# Revit family: Haworth_BeHold_Modular_SlimPedestal
name_source: partatom
category: Furniture Systems
revit_build: Autodesk Revit 2018 (Build: 20170223_1515(x64)
units: mm (PartAtom-declared; Revit-internal decimal feet)

## family parameters
Always vertical = Yes
Cut with Voids When Loaded = No
OmniClass Number = 23.40.70.14.64.21
OmniClass Title = Systems Furniture
Part Type = Normal
Room Calculation Point = No
Round Connector Dimension = Use Diameter
Shared = No
Work Plane-Based = No

## types (6) — shared parameters
Actual Leg Control = No
Actual Width = 12"
Assembly Code = E2020200
Back Case Back Control = 0"
Case Thickness = 3/4"
Caster Back Offset = 1 3/16"
Caster Finish = Haworth _ Polymer _ Slate
Caster Front Offset = 1 7/8"
Casters Side Offset = 1 9/16"
Custom Size = No
Drawer Height = 4 1/8"
Drawer Width = 10 9/32"
Glide Finish = Haworth _ Polymer _ Slate
Hinged Lock Offset = 1 3/4"
Leg Height = 6"
Manufacturer = Haworth
Max. Depth = 30"
Max. Height = 28"
Max. Width = 12"
Min. Depth = 16"
Min. Height = 20"
Min. Width = 12"
Model = Haworth Be_Hold
Pedestal Shelf Offset = 13 3/16"
Revision Number = 1
Size = Verify Final Dim. w/ Haworth
Sustainability Info = https://www.haworth.com
Top Case Back Control = 0"
URL = www.haworth.com
URL - Product = https://www.haworth.com
Warranty = http://www.haworth.com
With Leg = No
With Lock = Yes

## per-type parameters (varying)
- Attached - Drawer/Open - Proud Back - 30d: Actual Depth=30"; Actual Height=27 7/8"; Actual Mounting Height=0"; Actual Pedestal Shelf=Yes; Attached=Yes; Back Case Side Control=0"; Bottom Case Offset=1/2"; Case Height=27 3/8"; Depth=30"; Description=Haworth - Be_Hold - Slim Pedestal - Attached - Drawer/Open; Drawer and Open=Yes; Glide Control=Yes; Hinge Door Lock Control=No; Hinged Doors=No; Inset Style=No; Mobile=No; One and One Half High=No; Pedestal Shelf Depth=29 1/4"; Proud Style=Yes; Shelf=Yes; Side Case Back Control=3/4"; Side Case Front Control=0"; Standard Back=Proud Back or Inset Back; Standard Depths=16, 18, 24, 30 in.; Standard Heights=2H; Suspended=No; Suspended Height Control=0"; Top Case Front Control=1/8"; Top Hinged Door Dimension=1/8"; Top Thickness=1 31/256"; Top Visibility Control=Yes; Two High=Yes
- Attached - Hinged Door - Proud Back - 30d: Actual Depth=30"; Actual Height=27 7/8"; Actual Mounting Height=0"; Actual Pedestal Shelf=No; Attached=Yes; Back Case Side Control=0"; Bottom Case Offset=1/2"; Case Height=27 3/8"; Depth=30"; Description=Haworth - Be_Hold - Slim Pedestal - Attached - Hinged Door; Drawer and Open=No; Glide Control=Yes; Hinge Door Lock Control=Yes; Hinged Doors=Yes; Inset Style=No; Mobile=No; One and One Half High=No; Pedestal Shelf Depth=29 1/4"; Proud Style=Yes; Shelf=No; Side Case Back Control=3/4"; Side Case Front Control=3/4"; Standard Back=Proud Back or Inset Back; Standard Depths=16, 18, 24, 30 in.; Standard Heights=2H; Suspended=No; Suspended Height Control=0"; Top Case Front Control=3/4"; Top Hinged Door Dimension=1/8"; Top Thickness=1 31/256"; Top Visibility Control=Yes; Two High=Yes
- Suspended - Drawer/Open - Inset Back - 17d: Actual Depth=17"; Actual Height=20"; Actual Mounting Height=27 7/8"; Actual Pedestal Shelf=No; Attached=No; Back Case Side Control=3/4"; Bottom Case Offset=7 7/8"; Case Height=18"; Depth=17"; Description=Haworth - Be_Hold - Slim Pedestal - Suspended - Drawer/Open; Drawer and Open=Yes; Glide Control=No; Hinge Door Lock Control=No; Hinged Doors=No; Inset Style=Yes; Mobile=No; One and One Half High=Yes; Pedestal Shelf Depth=16 1/4"; Proud Style=No; Shelf=No; Side Case Back Control=0"; Side Case Front Control=0"; Standard Back=Inset Back; Standard Depths=17 in.; Standard Heights=1.5H; Suspended=Yes; Suspended Height Control=2"; Top Case Front Control=1/8"; Top Hinged Door Dimension=0"; Top Thickness=3/4"; Top Visibility Control=No; Two High=No
- Suspended - Hinged Door - Inset Back - 17d: Actual Depth=17"; Actual Height=20"; Actual Mounting Height=27 7/8"; Actual Pedestal Shelf=No; Attached=No; Back Case Side Control=3/4"; Bottom Case Offset=7 7/8"; Case Height=18"; Depth=17"; Description=Haworth - Be_Hold - Slim Pedestal - Suspended - Hinged Door; Drawer and Open=No; Glide Control=No; Hinge Door Lock Control=Yes; Hinged Doors=Yes; Inset Style=Yes; Mobile=No; One and One Half High=Yes; Pedestal Shelf Depth=16 1/4"; Proud Style=No; Shelf=No; Side Case Back Control=0"; Side Case Front Control=3/4"; Standard Back=Inset Back; Standard Depths=17 in.; Standard Heights=1.5H; Suspended=Yes; Suspended Height Control=2"; Top Case Front Control=3/4"; Top Hinged Door Dimension=0"; Top Thickness=3/4"; Top Visibility Control=No; Two High=No
- Mobile - Drawer/Open - Inset Back - 24d: Actual Depth=24"; Actual Height=21 1/4"; Actual Mounting Height=0"; Actual Pedestal Shelf=No; Attached=No; Back Case Side Control=3/4"; Bottom Case Offset=1 3/4"; Case Height=19 1/2"; Depth=24"; Description=Haworth - Be_Hold - Slim Pedestal - Mobile - Drawer/Open; Drawer and Open=Yes; Glide Control=No; Hinge Door Lock Control=No; Hinged Doors=No; Inset Style=Yes; Mobile=Yes; One and One Half High=Yes; Pedestal Shelf Depth=23 1/4"; Proud Style=No; Shelf=No; Side Case Back Control=0"; Side Case Front Control=0"; Standard Back=Inset Back; Standard Depths=18, 24 in.; Standard Heights=1.5H; Suspended=No; Suspended Height Control=0"; Top Case Front Control=1/8"; Top Hinged Door Dimension=0"; Top Thickness=3/4"; Top Visibility Control=No; Two High=No
- Mobile - Hinged Door - Inset Back - 24d: Actual Depth=24"; Actual Height=21 1/4"; Actual Mounting Height=0"; Actual Pedestal Shelf=No; Attached=No; Back Case Side Control=3/4"; Bottom Case Offset=1 3/4"; Case Height=19 1/2"; Depth=24"; Description=Haworth - Be_Hold - Slim Pedestal - Mobile - Hinged Door; Drawer and Open=No; Glide Control=No; Hinge Door Lock Control=Yes; Hinged Doors=Yes; Inset Style=Yes; Mobile=Yes; One and One Half High=Yes; Pedestal Shelf Depth=23 1/4"; Proud Style=No; Shelf=No; Side Case Back Control=0"; Side Case Front Control=3/4"; Standard Back=Inset Back; Standard Depths=18, 24 in.; Standard Heights=1.5H; Suspended=No; Suspended Height Control=0"; Top Case Front Control=3/4"; Top Hinged Door Dimension=0"; Top Thickness=3/4"; Top Visibility Control=No; Two High=No

## geometry (parser evidence)
native form markers: Sweep x8
no freeform markers — native parametric forms only
